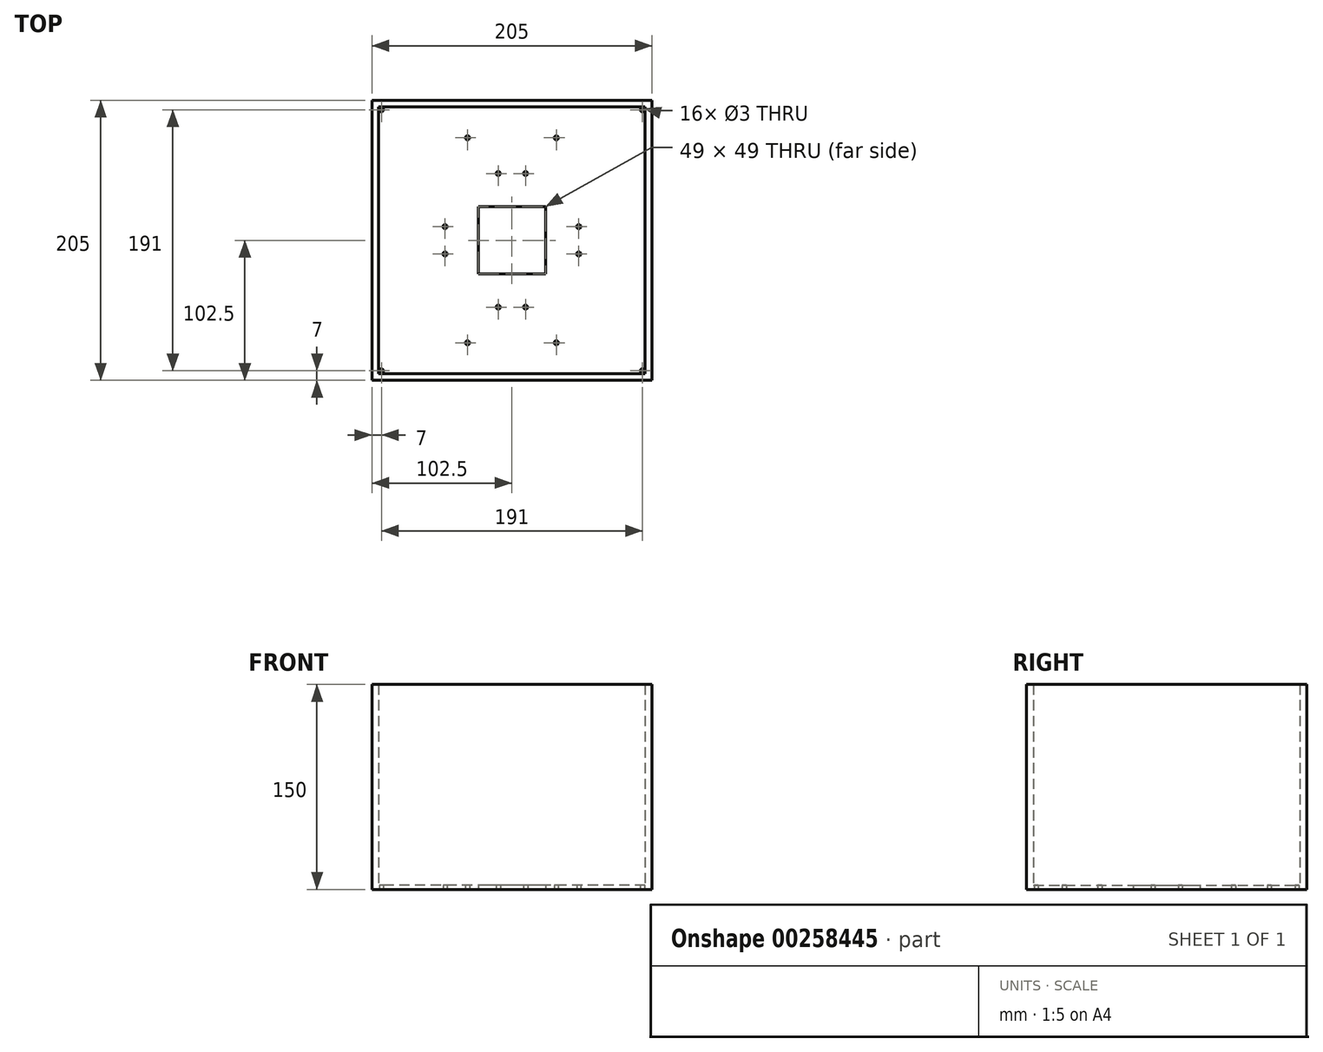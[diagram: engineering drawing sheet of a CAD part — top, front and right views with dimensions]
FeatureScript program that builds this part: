
annotation { "Feature Type Name" : "Feature", "Feature Type Description" : "" }
export const myFeature = defineFeature(function(context is Context, id is Id, definition is map)
    precondition{}
    {
        {
            var Q0;
            Q0=qCreatedBy(makeId("Top.planeOp"),FACE);
            var sketch = newSketch(context, id + "F0", { "sketchPlane" : qUnion([Q0])});
            skLineSegment(sketch, "E0.bottom", {"start": v(97.5, -97.5) * mm, "end": v(-97.5, -97.5) * mm});
            skLineSegment(sketch, "E0.top", {"start": v(97.5, 97.5) * mm, "end": v(-97.5, 97.5) * mm});
            skLineSegment(sketch, "E0.left", {"start": v(97.5, -97.5) * mm, "end": v(97.5, 97.5) * mm});
            skLineSegment(sketch, "E0.right", {"start": v(-97.5, -97.5) * mm, "end": v(-97.5, 97.5) * mm});
            skPoint(sketch, "E0.middle", {"position": v(0, 0) * mm});
            skLineSegment(sketch, "E1", {"start": v(-97.5, 0) * mm, "end": v(97.5, 0) * mm, "construction": true});
            skLineSegment(sketch, "E2", {"start": v(0, -97.5) * mm, "end": v(0, 97.5) * mm, "construction": true});
            skLineSegment(sketch, "E3", {"start": v(-97.5, 97.5) * mm, "end": v(97.5, -97.5) * mm, "construction": true});
            skLineSegment(sketch, "E4", {"start": v(97.5, 97.5) * mm, "end": v(-97.5, -97.5) * mm, "construction": true});
            skCircle(sketch, "E5", {"center": v(10, 48.9) * mm, "radius": 1.5 * mm});
            skCircle(sketch, "E6.MirrorC", {"center": v(48.9, 10) * mm, "radius": 1.5 * mm});
            skCircle(sketch, "E7.MirrorC", {"center": v(-10, 48.9) * mm, "radius": 1.5 * mm});
            skCircle(sketch, "E8.MirrorC", {"center": v(-48.9, 10) * mm, "radius": 1.5 * mm});
            skCircle(sketch, "E9.MirrorC", {"center": v(-48.9, -10) * mm, "radius": 1.5 * mm});
            skCircle(sketch, "E10.MirrorC", {"center": v(-10, -48.9) * mm, "radius": 1.5 * mm});
            skCircle(sketch, "E11.MirrorC", {"center": v(10, -48.9) * mm, "radius": 1.5 * mm});
            skCircle(sketch, "E12.MirrorC", {"center": v(48.9, -10) * mm, "radius": 1.5 * mm});
            skLineSegment(sketch, "E13.0", {"start": v(102.5, -102.5) * mm, "end": v(-102.5, -102.5) * mm});
            skLineSegment(sketch, "E13.1", {"start": v(102.5, -102.5) * mm, "end": v(102.5, 102.5) * mm});
            skLineSegment(sketch, "E13.2", {"start": v(102.5, 102.5) * mm, "end": v(-102.5, 102.5) * mm});
            skLineSegment(sketch, "E13.3", {"start": v(-102.5, -102.5) * mm, "end": v(-102.5, 102.5) * mm});
            skLineSegment(sketch, "E14.0", {"start": v(24.5, 24.5) * mm, "end": v(-24.5, 24.5) * mm});
            skLineSegment(sketch, "E14.1", {"start": v(24.5, -24.5) * mm, "end": v(24.5, 24.5) * mm});
            skLineSegment(sketch, "E14.2", {"start": v(24.5, -24.5) * mm, "end": v(-24.5, -24.5) * mm});
            skLineSegment(sketch, "E14.3", {"start": v(-24.5, -24.5) * mm, "end": v(-24.5, 24.5) * mm});
            skCircle(sketch, "E15", {"center": v(-95.5, 95.5) * mm, "radius": 1.5 * mm});
            skCircle(sketch, "E16.MirrorC", {"center": v(95.5, 95.5) * mm, "radius": 1.5 * mm});
            skCircle(sketch, "E17.MirrorC", {"center": v(-95.5, -95.5) * mm, "radius": 1.5 * mm});
            skCircle(sketch, "E18.MirrorC", {"center": v(95.5, -95.5) * mm, "radius": 1.5 * mm});
            skCircle(sketch, "E19", {"center": v(-32.5, 75) * mm, "radius": 1.5 * mm});
            skCircle(sketch, "E20.MirrorC", {"center": v(32.5, 75) * mm, "radius": 1.5 * mm});
            skCircle(sketch, "E21.MirrorC", {"center": v(32.5, -75) * mm, "radius": 1.5 * mm});
            skCircle(sketch, "E22.MirrorC", {"center": v(-32.5, -75) * mm, "radius": 1.5 * mm});
            skSolve(sketch);
        }
        {
            var Q0;
            Q0=makeQuery(id+"F0.imprint","IMPRINT",FACE,{"disambiguationData":[TD([[makeQuery(id+"F0.imprint","IMPRINT",EDGE,{"derivedFrom":sQuery(id+"F0.wireOp",EDGE,"E0.bottom")}),1.0]])]});
            extrude(context, id + "F1", {"entities" : qUnion([Q0]), "depth" : 150 * mm});
        }
        {
            var Q0;
            Q0=makeQuery(id+"F0.imprint","IMPRINT",FACE,{"disambiguationData":[TD([[makeQuery(id+"F0.imprint","IMPRINT",EDGE,{"derivedFrom":sQuery(id+"F0.wireOp",EDGE,"E0.bottom")}),-1.0]])]});
            extrude(context, id + "F2", {"entities" : qUnion([Q0]), "operationType" : NewBodyOperationType.ADD, "depth" : 3 * mm});
        }
    });
